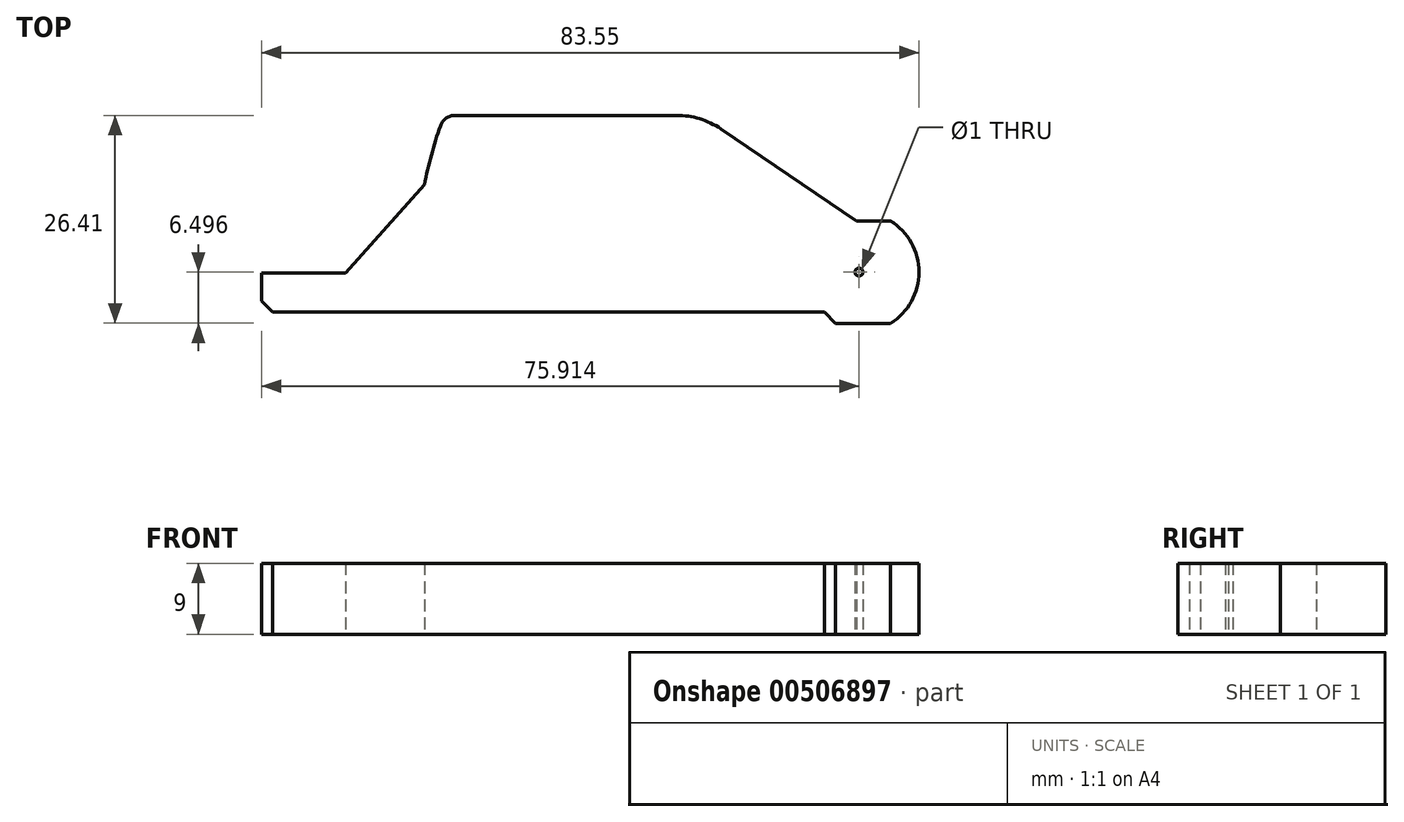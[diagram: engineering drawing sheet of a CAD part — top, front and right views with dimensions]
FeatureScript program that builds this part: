
annotation { "Feature Type Name" : "Feature", "Feature Type Description" : "" }
export const myFeature = defineFeature(function(context is Context, id is Id, definition is map)
    precondition{}
    {
        {
            var Q0;
            Q0=qCreatedBy(makeId("Top.planeOp"),FACE);
            var sketch = newSketch(context, id + "F0", { "sketchPlane" : qUnion([Q0])});
            skLineSegment(sketch, "E0", {"start": v(-34.34, 0) * mm, "end": v(35.75, 0) * mm});
            skLineSegment(sketch, "E1", {"start": v(-35.75, 1.41) * mm, "end": v(-35.75, 5) * mm});
            skLineSegment(sketch, "E2", {"start": v(-35.75, 5) * mm, "end": v(-25.05, 5) * mm});
            skLineSegment(sketch, "E3", {"start": v(-35.75, 1.41) * mm, "end": v(-34.34, 0) * mm});
            skPoint(sketch, "E4.orphan", {"position": v(-35.75, 0) * mm});
            skLineSegment(sketch, "E5", {"start": v(35.75, 0) * mm, "end": v(37.16, -1.41) * mm});
            skLineSegment(sketch, "E6", {"start": v(-25.05, 5) * mm, "end": v(-15.05, 16.18) * mm});
            skLineSegment(sketch, "E7", {"start": v(-15.05, 16.18) * mm, "end": v(-15.05, 2.64) * mm, "construction": true});
            skLineSegment(sketch, "E8", {"start": v(-25.05, 5) * mm, "end": v(-29.52, 0) * mm});
            skLineSegment(sketch, "E9", {"start": v(-11.11, 25) * mm, "end": v(17, 25) * mm});
            skLineSegment(sketch, "E10", {"start": v(37.16, -1.41) * mm, "end": v(44.16, -1.41) * mm});
            skLineSegment(sketch, "E11", {"start": v(44.16, 11.59) * mm, "end": v(39.84, 11.59) * mm});
            skCircle(sketch, "E12", {"center": v(40.16, 5.09) * mm, "radius": 1.93 * mm});
            skArc(sketch, "E13", {"start": v(44.16, 11.59) * mm, "mid": v(47.8, 5.09) * mm, "end": v(44.16, -1.41) * mm});
            skLineSegment(sketch, "E14", {"start": v(22.61, 23.28) * mm, "end": v(39.84, 11.59) * mm});
            skArc(sketch, "E15", {"start": v(-13, 23.66) * mm, "mid": v(-14.16, 19.96) * mm, "end": v(-15.05, 16.18) * mm});
            skPoint(sketch, "E16.visualSharp", {"position": v(-12.52, 25) * mm});
            skArc(sketch, "E16.filletArc", {"start": v(-11.11, 25) * mm, "mid": v(-12.27, 24.63) * mm, "end": v(-13, 23.66) * mm});
            skLineSegment(sketch, "E17", {"start": v(1, 25) * mm, "end": v(1, 22.5) * mm});
            skLineSegment(sketch, "E18", {"start": v(1, 22.5) * mm, "end": v(2.25, 22.5) * mm});
            skLineSegment(sketch, "E19", {"start": v(2.25, 22.5) * mm, "end": v(2.25, 25) * mm});
            skPoint(sketch, "E20.visualSharp", {"position": v(20.07, 25) * mm});
            skArc(sketch, "E20.filletArc", {"start": v(22.61, 23.28) * mm, "mid": v(19.93, 24.56) * mm, "end": v(17, 25) * mm});
            skCircle(sketch, "E21", {"center": v(40.16, 5.09) * mm, "radius": 0.5 * mm});
            skLineSegment(sketch, "E22", {"start": v(-0.75, 0) * mm, "end": v(-0.75, 4) * mm});
            skLineSegment(sketch, "E23", {"start": v(-3.75, 7) * mm, "end": v(-23.26, 7) * mm});
            skPoint(sketch, "E24.visualSharp", {"position": v(-0.75, 7) * mm});
            skArc(sketch, "E24.filletArc", {"start": v(-0.75, 4) * mm, "mid": v(-1.63, 6.12) * mm, "end": v(-3.75, 7) * mm});
            skLineSegment(sketch, "E25", {"start": v(-9.53, 21) * mm, "end": v(18.02, 16) * mm});
            skLineSegment(sketch, "E26", {"start": v(18.02, 16) * mm, "end": v(24.06, 8.03) * mm});
            skSolve(sketch);
        }
        {
            var Q0;
            Q0 = qSketchRegion(id + "F0", true);
            var Q1;
            Q1=makeQuery(id+"F0.imprint","IMPRINT",FACE,{"disambiguationData":[TD([[makeQuery(id+"F0.imprint","IMPRINT",EDGE,{"derivedFrom":sQuery(id+"F0.wireOp",EDGE,"E12")}),1.0]])]});
            extrude(context, id + "F1", {"entities" : qUnion([Q0, Q1]), "depth" : 9 * mm});
        }
    });
